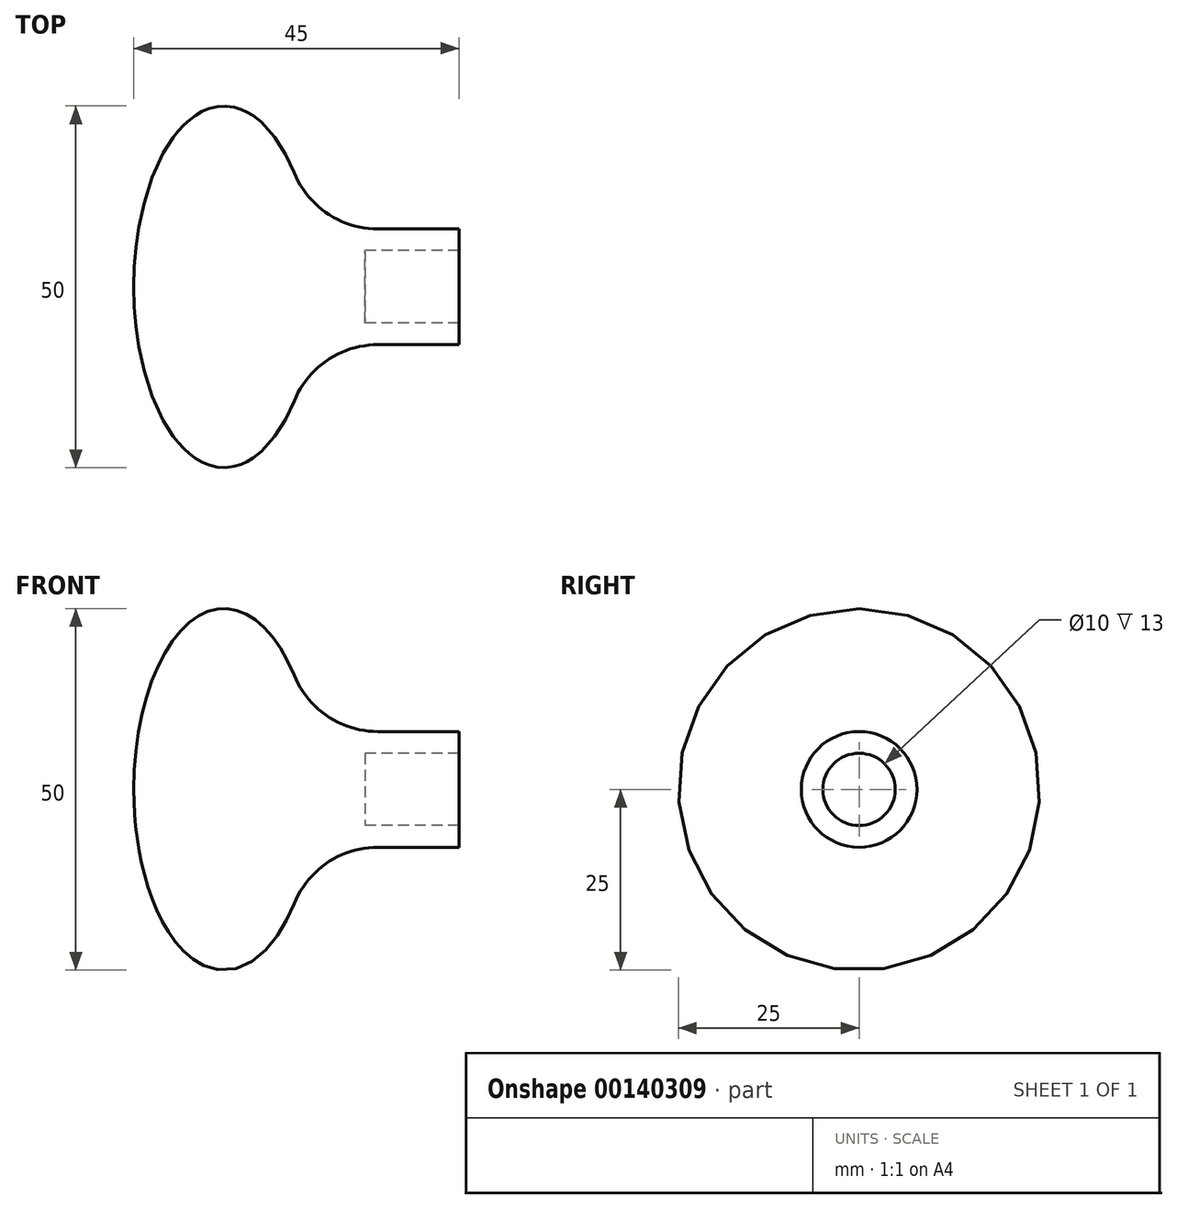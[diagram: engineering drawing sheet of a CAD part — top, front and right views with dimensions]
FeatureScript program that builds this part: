
annotation { "Feature Type Name" : "Feature", "Feature Type Description" : "" }
export const myFeature = defineFeature(function(context is Context, id is Id, definition is map)
    precondition{}
    {
        {
            var Q0;
            Q0=qCreatedBy(makeId("Front.planeOp"),FACE);
            var sketch = newSketch(context, id + "F0", { "sketchPlane" : qUnion([Q0])});
            skLineSegment(sketch, "E0", {"start": v(-45, 0) * mm, "end": v(-13, 0) * mm});
            skLineSegment(sketch, "E1", {"start": v(-13, 0) * mm, "end": v(-13, 5) * mm});
            skLineSegment(sketch, "E2", {"start": v(-13, 5) * mm, "end": v(0, 5) * mm});
            skEllipticalArc(sketch, "E3", {});
            skLineSegment(sketch, "E4", {"start": v(-20.66, 8) * mm, "end": v(0, 8) * mm});
            skLineSegment(sketch, "E5", {"start": v(0, 8) * mm, "end": v(0, 5) * mm});
            const initialGuessF0  = {"E3": [-0.0325, 0, 0, 1, 0.025, 0.0125, 5.03811846767932, 1.5707963267948966]};
            skSetInitialGuess(sketch, initialGuessF0);
            skSolve(sketch);
        }
        {
            var Q0;
            Q0=makeQuery(id+"F0.imprint","IMPRINT",FACE,{"disambiguationData":[TD([[makeQuery(id+"F0.imprint","IMPRINT",EDGE,{"derivedFrom":sQuery(id+"F0.wireOp",EDGE,"E0")}),1.0]])]});
            var Q1;
            Q1=sQuery(id+"F0.wireOp",EDGE,"E0");
            revolve(context, id + "F1", {"entities" : qUnion([Q0]), "axis" : qUnion([Q1]), "revolveType" : RevolveType.FULL});
        }
        {
            var Q0;
            Q0=makeQuery(id+"F1.opRevolve","SWEPT_EDGE",EDGE,{"disambiguationData":[OSD([sQuery(id+"F0.wireOp",EDGE,"E3"),sQuery(id+"F0.wireOp",EDGE,"E4")])]});
            fillet(context, id + "F2", {"entities" : qUnion([Q0]), "radius" : 12.5 * mm, "tangentPropagation" : true, "allowEdgeOverflow" : false});
        }
    });
